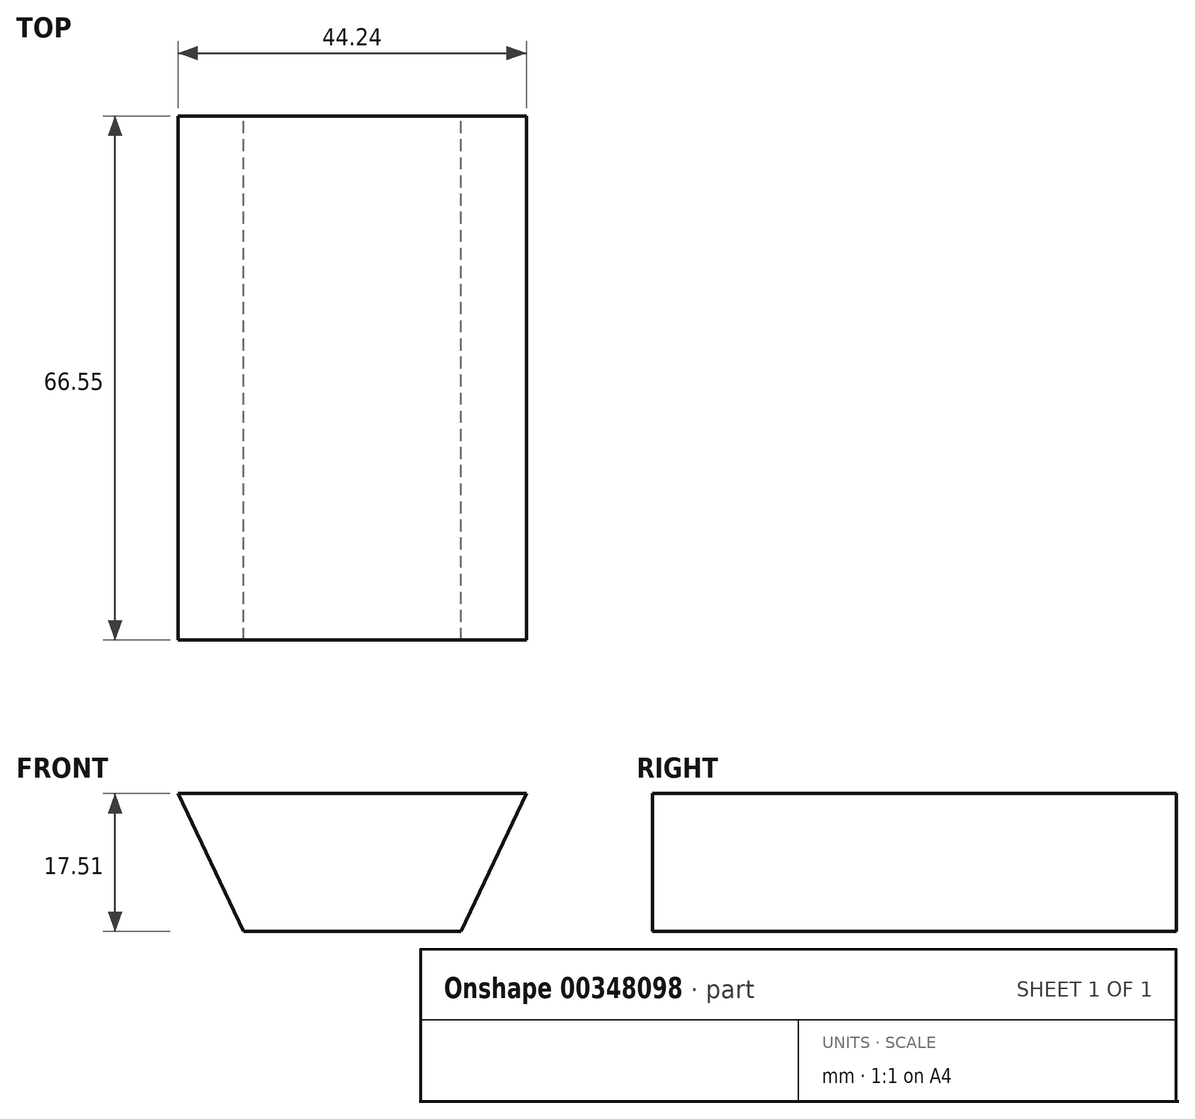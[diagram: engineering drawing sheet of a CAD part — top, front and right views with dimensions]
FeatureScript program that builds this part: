
annotation { "Feature Type Name" : "Feature", "Feature Type Description" : "" }
export const myFeature = defineFeature(function(context is Context, id is Id, definition is map)
    precondition{}
    {
        {
            var Q0;
            Q0=qCreatedBy(makeId("Front.planeOp"),FACE);
            var sketch = newSketch(context, id + "F0", { "sketchPlane" : qUnion([Q0])});
            skLineSegment(sketch, "E0", {"start": v(0, -17.51) * mm, "end": v(-13.83, -17.51) * mm});
            skLineSegment(sketch, "E1", {"start": v(-13.83, -17.51) * mm, "end": v(-22.12, 0) * mm});
            skLineSegment(sketch, "E2", {"start": v(-22.12, 0) * mm, "end": v(0, 0) * mm});
            skLineSegment(sketch, "E3.MirrorCS", {"start": v(22.12, 0) * mm, "end": v(0, 0) * mm});
            skLineSegment(sketch, "E4.MirrorCS", {"start": v(13.83, -17.51) * mm, "end": v(22.12, 0) * mm});
            skLineSegment(sketch, "E5.MirrorCS", {"start": v(0, -17.51) * mm, "end": v(13.83, -17.51) * mm});
            skSolve(sketch);
        }
        {
            var Q0;
            Q0=qCreatedBy(makeId("Front.planeOp"),FACE);
            var sketch = newSketch(context, id + "F1", { "sketchPlane" : qUnion([Q0])});
            skSolve(sketch);
        }
        {
            var Q0;
            Q0 = qSketchRegion(id + "F1", true);
            var Q1;
            Q1=makeQuery(id+"F0.imprint","IMPRINT",FACE,{"disambiguationData":[TD([[makeQuery(id+"F0.imprint","IMPRINT",EDGE,{"derivedFrom":sQuery(id+"F0.wireOp",EDGE,"E0")}),-1.0]])]});
            extrude(context, id + "F2", {"entities" : qUnion([Q0, Q1]), "depth" : 66.55 * mm});
        }
    });
